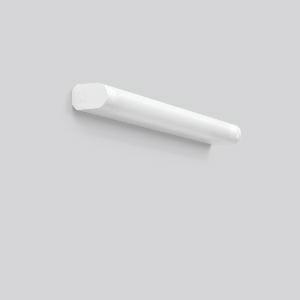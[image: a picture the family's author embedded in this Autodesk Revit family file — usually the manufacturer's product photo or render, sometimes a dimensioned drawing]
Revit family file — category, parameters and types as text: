
# Revit family: rt_44_451174_002_1_9c84
name_source: partatom
category: Lighting Fixtures
units: mm (PartAtom-declared; Revit-internal decimal feet)

## family parameters
Cut with Voids When Loaded = No
Host = Face
Light Source = No
Part Type = Normal
Room Calculation Point = No
Round Connector Dimension = Use Diameter
Shared = No

## types (1)
- RT 44 (1 x LED Modul 840, 970 lm, 4000)
    Apparent Load = 10 VA
    CIE Flux Codes = 36 64 85 81 100
    Color Rendering = 80
    Color Temperature = 4000
    Default Elevation = 1800 mm
    Description = Series: RT 44
Linear luminaire, can be used as wall and mirror luminaire. Base: aluminium, powder-coated. End caps: plastic (polycarbonate), shock-resistant. Diffuser: plastic (polycarbonate), opal. Suitable for Ceiling mounting, Wall (surface). Can be installed horizontally and vertically. Very easy installation thanks to Plug+Play connection. With push button switch and Schukoplug socket. Driver integrated. High type of protection: IP44 for use in wet areas. 
Colour: pure white (RAL 9010)
Length: 721 mm
Width: 55 mm
Height: 87 mm
Lamp: LED
Socket: without socket
Colour temperature: 4000K
Colour rendering index (CRI): 80
System power: 10 W
Rated luminous flux: 970 lm
Luminous efficiency: 97 lm/W
Control gear: Regulated power supply
Protection class: I
Type of protection: IP 44
    Height = 87 mm
    Lamp = 1 x LED Modul 840
    Lamp Light Flux = 970 lm
    Lamp count = 1
    Length = 721 mm
    Lifetime = 50000 h
    Luminous efficacy = 97 lm/W
    Manufacturer = RZB
    ModVariant = No
    Model = 451174.002.1
    Mounting Place = Ceiling, Wall
    Mounting Type = Surface mounted
    Number of Poles = 1
    OnlyDefault = Yes
    Power Factor = 1
    Product Name = RT 44
    Product group = Surface mounted ceiling and wall luminaires
    ProductGroupID = 305
    Protection Class = Protection class I
    Protection Degree = IP 44
    RLX_Detail_Level = 1
    RLX_Emergency_Light_Flux = 0 lm
    RLX_Emergency_Type = 0
    RLX_Emergency_Type_DB = No
    RlxData = <blob elided: 25941 chars, md5=de594469>
    Socket = socket
    Standby Power = 0 W
    System Light Flux = 970 lm
    System Power = 10 W
    Type Comments = Product without accessories
    Type Image = 451060.752.jpg
    URL = http://relux.com
    VarID = ---
    Voltage = 230 V
    Voltage Range = 220-240 V
    Weight = 0.00 kg
    Width = 55 mm

## geometry (parser evidence)
native form markers: Blend x4, Sweep x12
no freeform markers — native parametric forms only
